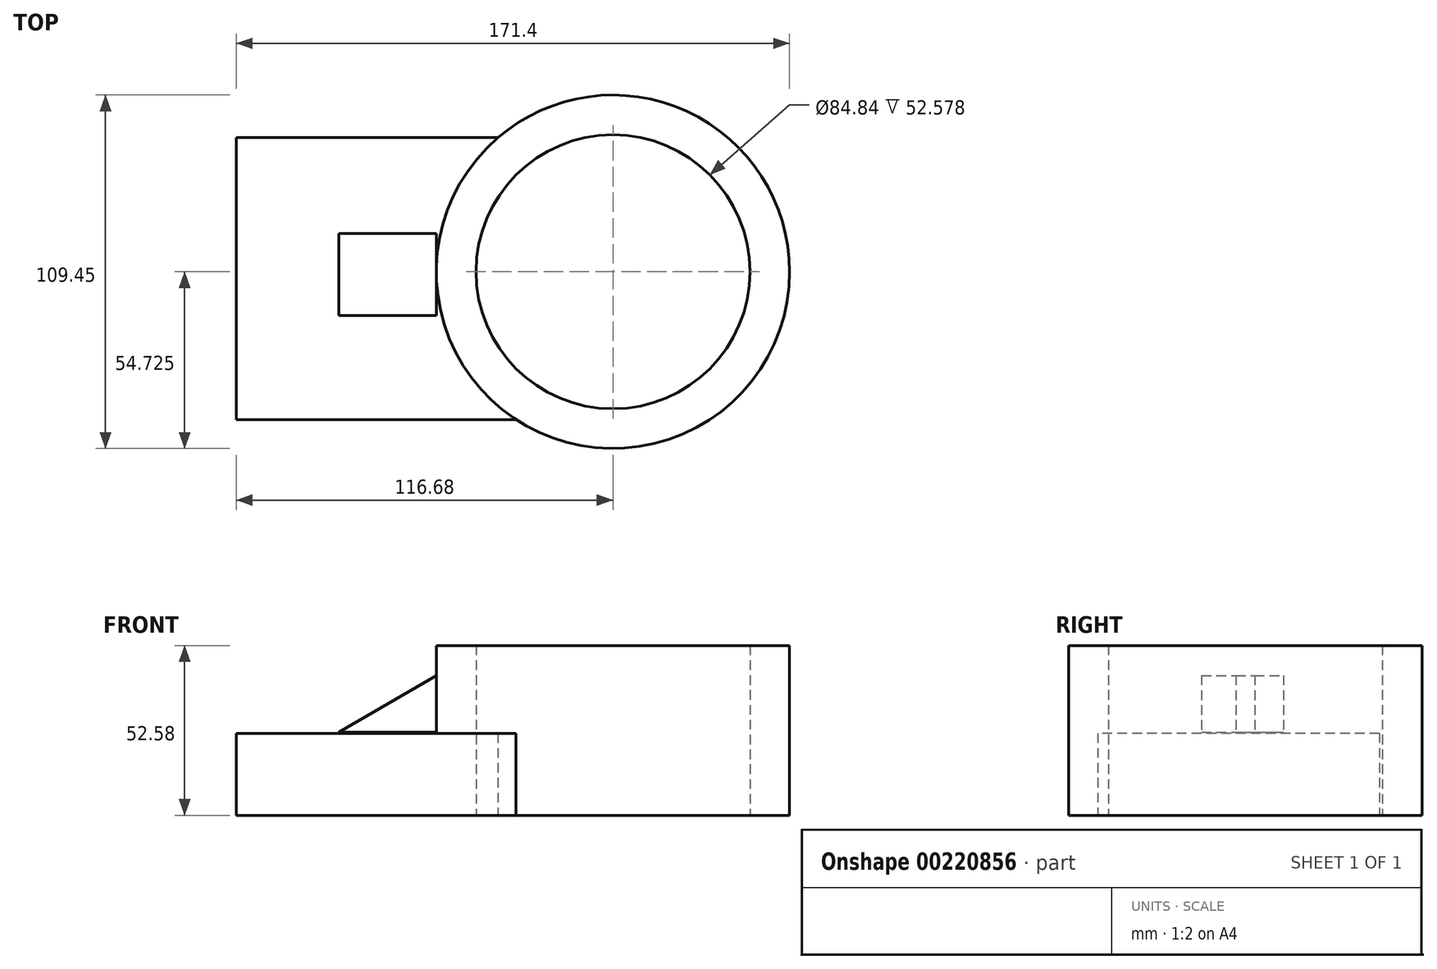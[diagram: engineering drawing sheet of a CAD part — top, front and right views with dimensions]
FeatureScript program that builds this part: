
annotation { "Feature Type Name" : "Feature", "Feature Type Description" : "" }
export const myFeature = defineFeature(function(context is Context, id is Id, definition is map)
    precondition{}
    {
        {
            var Q0;
            Q0=qCreatedBy(makeId("Top.planeOp"),FACE);
            var sketch = newSketch(context, id + "F0", { "sketchPlane" : qUnion([Q0])});
            skLineSegment(sketch, "E0.bottom", {"start": v(-116.68, 29.7) * mm, "end": v(-14.65, 29.7) * mm});
            skLineSegment(sketch, "E0.top", {"start": v(-116.68, -57.6) * mm, "end": v(-14.65, -57.6) * mm});
            skLineSegment(sketch, "E0.left", {"start": v(-116.68, 29.7) * mm, "end": v(-116.68, -57.6) * mm});
            skLineSegment(sketch, "E0.right", {"start": v(-14.65, 29.7) * mm, "end": v(-14.65, -57.6) * mm});
            skCircle(sketch, "E1", {"center": v(0, -11.84) * mm, "radius": 42.42 * mm});
            skCircle(sketch, "E2", {"center": v(0, -11.84) * mm, "radius": 54.72 * mm});
            skSolve(sketch);
        }
        {
            var Q0;
            {var subQ0=sQuery(id+"F0.wireOp",EDGE,"E0.right");var subQ5=sQuery(id+"F0.wireOp",EDGE,"E0.bottom");var subQ6=makeQuery(id+"F0.imprint","INTERSECT",VERTEX,{"derivedFrom":[subQ5,subQ0]});Q0=makeQuery(id+"F0.imprint","IMPRINT",FACE,{"disambiguationData":[TD([[makeQuery(id+"F0.imprint","IMPRINT",EDGE,{"disambiguationData":[TD([[subQ6,1.0]])],"derivedFrom":subQ5}),1.0]])]});}
            var Q1;
            {var subQ0=sQuery(id+"F0.wireOp",EDGE,"E0.right");var subQ5=sQuery(id+"F0.wireOp",EDGE,"E0.bottom");var subQ6=makeQuery(id+"F0.imprint","INTERSECT",VERTEX,{"derivedFrom":[subQ5,subQ0]});Q1=makeQuery(id+"F0.imprint","IMPRINT",FACE,{"disambiguationData":[TD([[makeQuery(id+"F0.imprint","IMPRINT",EDGE,{"disambiguationData":[TD([[subQ6,1.0]])],"derivedFrom":subQ5}),-1.0]])]});}
            extrude(context, id + "F1", {"entities" : qUnion([Q0, Q1]), "depth" : 52.58 * mm});
        }
        {
            var Q0;
            Q0 = qSketchRegion(id + "F0", true);
            extrude(context, id + "F2", {"entities" : qUnion([Q0]), "operationType" : NewBodyOperationType.ADD, "depth" : 25.4 * mm});
        }
        {
            var Q0;
            Q0=qCreatedBy(makeId("Front.planeOp"),FACE);
            var sketch = newSketch(context, id + "F3", { "sketchPlane" : qUnion([Q0])});
            skLineSegment(sketch, "E3.bottom", {"start": v(-54.65, 43.3) * mm, "end": v(-84.9, 43.3) * mm});
            skLineSegment(sketch, "E3.top", {"start": v(-54.65, 25.75) * mm, "end": v(-84.9, 25.75) * mm});
            skLineSegment(sketch, "E3.left", {"start": v(-54.65, 43.3) * mm, "end": v(-54.65, 25.75) * mm});
            skLineSegment(sketch, "E3.right", {"start": v(-84.9, 43.3) * mm, "end": v(-84.9, 25.75) * mm});
            skLineSegment(sketch, "E4", {"start": v(-54.65, 43.3) * mm, "end": v(-84.9, 25.75) * mm});
            skSolve(sketch);
        }
        {
            var Q0;
            Q0=makeQuery(id+"F3.imprint","IMPRINT",FACE,{"disambiguationData":[TD([[makeQuery(id+"F3.imprint","IMPRINT",EDGE,{"derivedFrom":sQuery(id+"F3.wireOp",EDGE,"E3.top")}),-1.0]])]});
            extrude(context, id + "F4", {"entities" : qUnion([Q0]), "operationType" : NewBodyOperationType.ADD, "depth" : 25.4 * mm});
        }
    });
